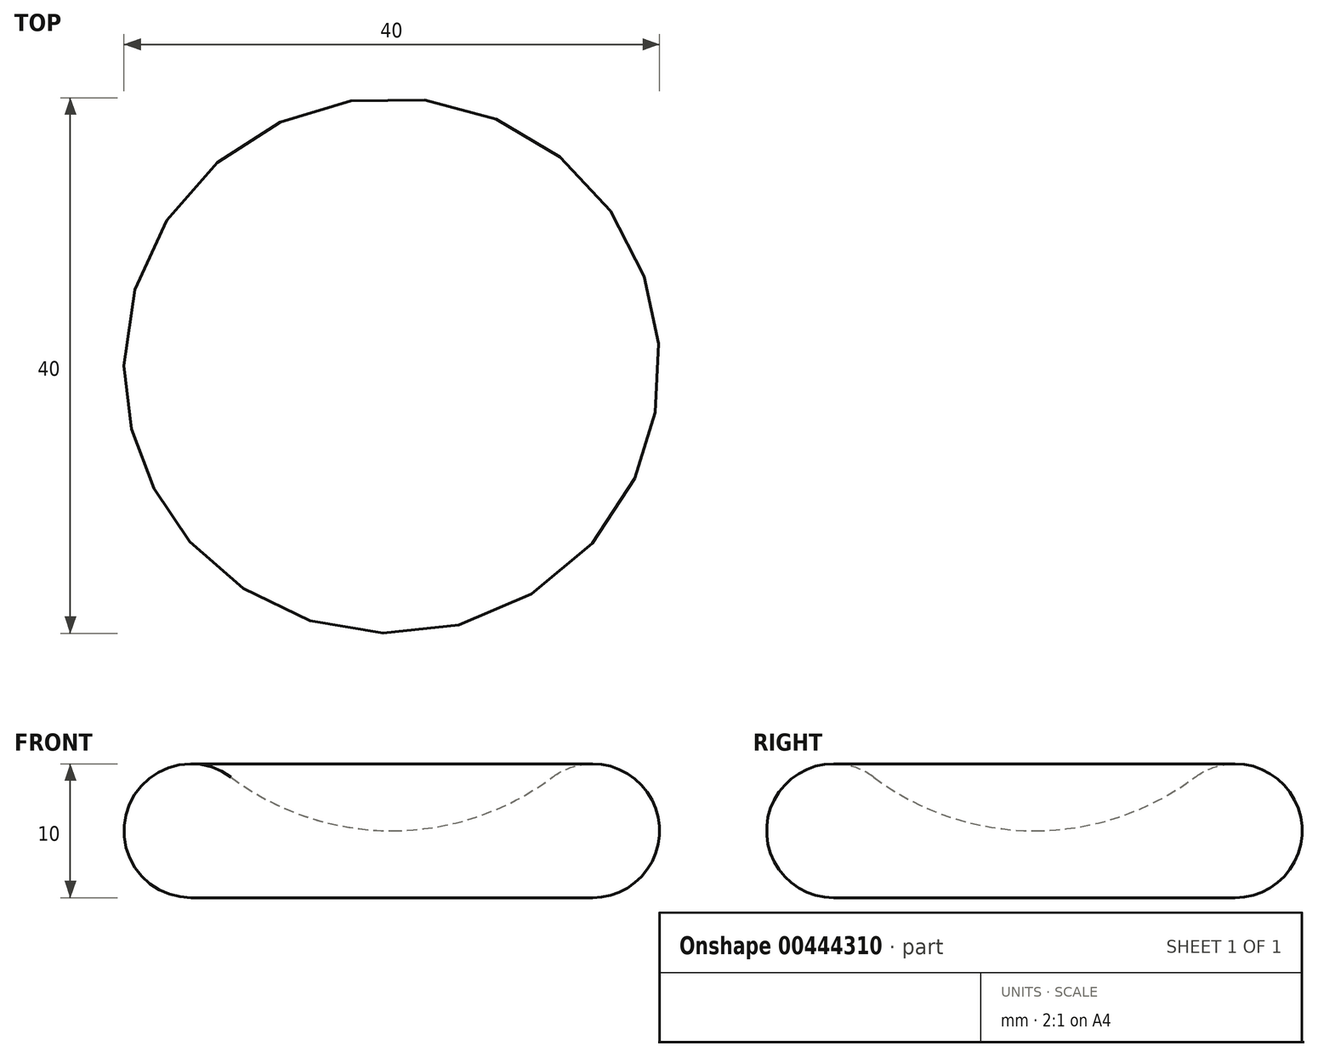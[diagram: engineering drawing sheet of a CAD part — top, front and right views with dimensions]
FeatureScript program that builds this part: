
annotation { "Feature Type Name" : "Feature", "Feature Type Description" : "" }
export const myFeature = defineFeature(function(context is Context, id is Id, definition is map)
    precondition{}
    {
        {
            var Q0;
            Q0=qCreatedBy(makeId("Front.planeOp"),FACE);
            var sketch = newSketch(context, id + "F0", { "sketchPlane" : qUnion([Q0])});
            skArc(sketch, "E0", {"start": v(-12, 9) * mm, "mid": v(-19.74, 6.58) * mm, "end": v(-15, 0) * mm});
            skArc(sketch, "E1", {"start": v(-12, 9) * mm, "mid": v(-6.32, 6.03) * mm, "end": v(0, 5) * mm});
            skLineSegment(sketch, "E2", {"start": v(-15, 0) * mm, "end": v(0, 0) * mm});
            skLineSegment(sketch, "E3", {"start": v(0, 0) * mm, "end": v(0, 5) * mm});
            skPoint(sketch, "E4.orphan", {"position": v(-19.46, 0) * mm});
            skSolve(sketch);
        }
        {
            var Q0;
            Q0=makeQuery(id+"F0.imprint","IMPRINT",FACE,{"disambiguationData":[TD([[makeQuery(id+"F0.imprint","IMPRINT",EDGE,{"derivedFrom":sQuery(id+"F0.wireOp",EDGE,"E0")}),1.0]])]});
            var Q1;
            Q1=sQuery(id+"F0.wireOp",EDGE,"E3");
            revolve(context, id + "F1", {"entities" : qUnion([Q0]), "axis" : qUnion([Q1]), "revolveType" : RevolveType.FULL});
        }
    });
